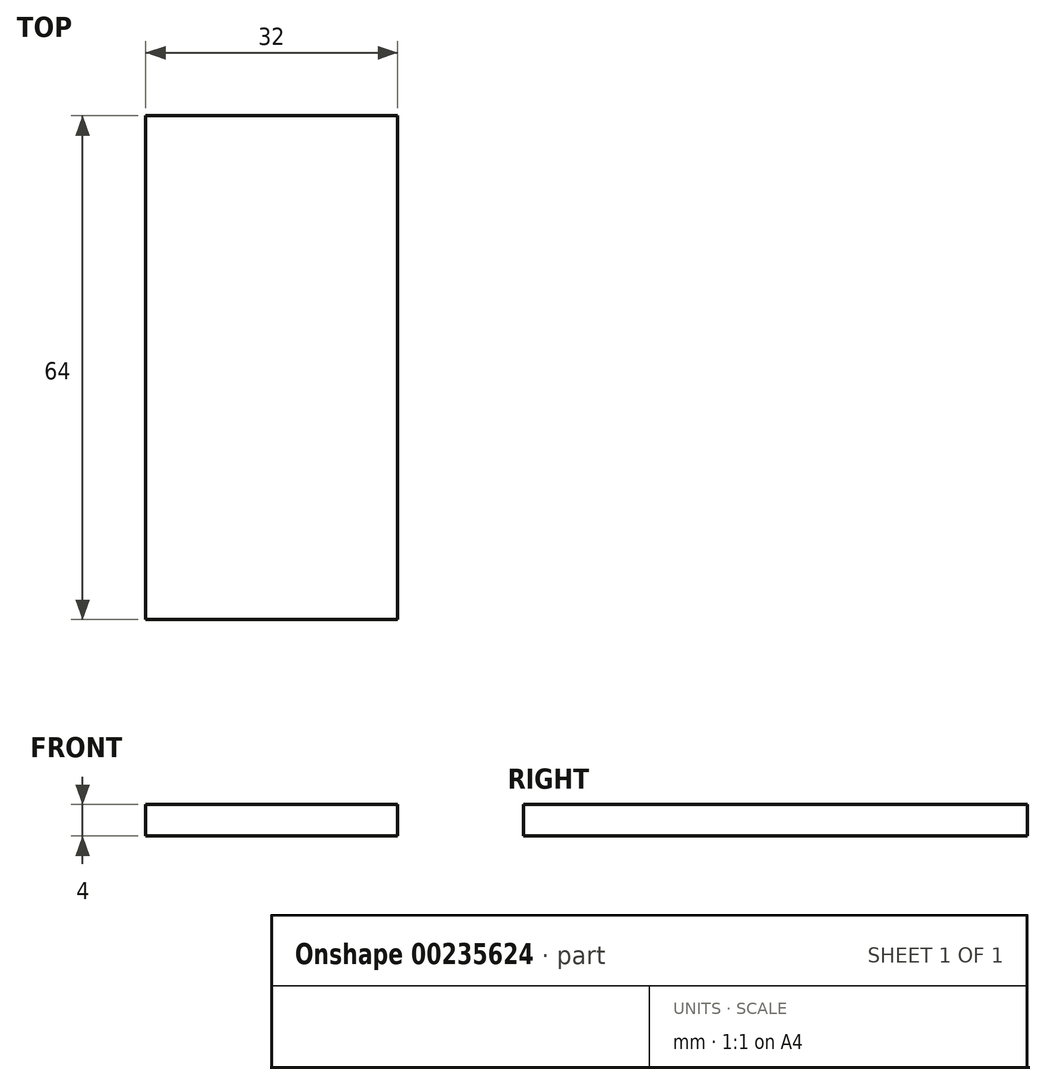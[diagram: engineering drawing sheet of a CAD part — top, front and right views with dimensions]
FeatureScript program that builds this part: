
annotation { "Feature Type Name" : "Feature", "Feature Type Description" : "" }
export const myFeature = defineFeature(function(context is Context, id is Id, definition is map)
    precondition{}
    {
        {
            var Q0;
            Q0=qCreatedBy(makeId("Top.planeOp"),FACE);
            var sketch = newSketch(context, id + "F0", { "sketchPlane" : qUnion([Q0])});
            skLineSegment(sketch, "E0.bottom", {"start": v(16, -32) * mm, "end": v(-16, -32) * mm});
            skLineSegment(sketch, "E0.top", {"start": v(16, 32) * mm, "end": v(-16, 32) * mm});
            skLineSegment(sketch, "E0.left", {"start": v(16, -32) * mm, "end": v(16, 32) * mm});
            skLineSegment(sketch, "E0.right", {"start": v(-16, -32) * mm, "end": v(-16, 32) * mm});
            skPoint(sketch, "E0.middle", {"position": v(0, 0) * mm});
            skSolve(sketch);
        }
        {
            var Q0;
            Q0=makeQuery(id+"F0.imprint","IMPRINT",FACE,{"disambiguationData":[TD([[makeQuery(id+"F0.imprint","IMPRINT",EDGE,{"derivedFrom":sQuery(id+"F0.wireOp",EDGE,"E0.bottom")}),-1.0]])]});
            extrude(context, id + "F1", {"entities" : qUnion([Q0]), "depth" : 4 * mm});
        }
    });
